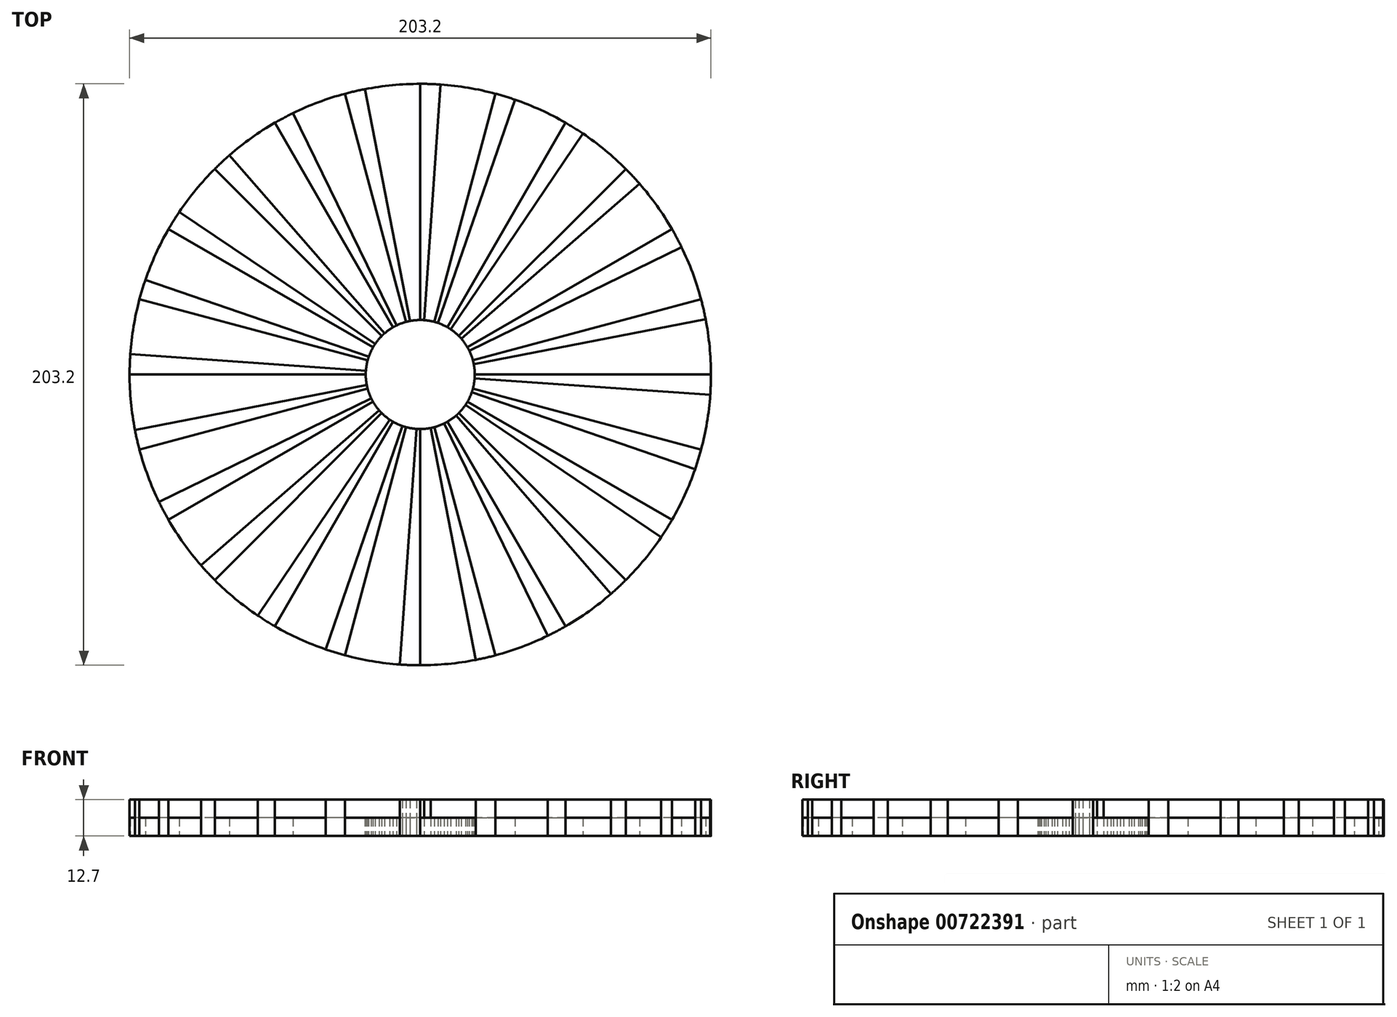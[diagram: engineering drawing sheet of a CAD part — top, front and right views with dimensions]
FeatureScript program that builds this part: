
annotation { "Feature Type Name" : "Feature", "Feature Type Description" : "" }
export const myFeature = defineFeature(function(context is Context, id is Id, definition is map)
    precondition{}
    {
        {
            var Q0;
            Q0=qCreatedBy(makeId("Top.planeOp"),FACE);
            var sketch = newSketch(context, id + "F0", { "sketchPlane" : qUnion([Q0])});
            skCircle(sketch, "E0", {"center": v(0, 0) * mm, "radius": 101.6 * mm});
            skLineSegment(sketch, "E1", {"start": v(0, 0) * mm, "end": v(0, 101.6) * mm});
            skLineSegment(sketch, "E2.1.0", {"start": v(0, 0) * mm, "end": v(-26.3, 98.14) * mm});
            skLineSegment(sketch, "E2.2.0", {"start": v(0, 0) * mm, "end": v(-50.8, 87.99) * mm});
            skLineSegment(sketch, "E2.3.0", {"start": v(0, 0) * mm, "end": v(-71.84, 71.84) * mm});
            skLineSegment(sketch, "E2.4.0", {"start": v(0, 0) * mm, "end": v(-87.99, 50.8) * mm});
            skLineSegment(sketch, "E2.5.0", {"start": v(0, 0) * mm, "end": v(-98.14, 26.3) * mm});
            skLineSegment(sketch, "E2.6.0", {"start": v(0, 0) * mm, "end": v(-101.6, 0) * mm});
            skLineSegment(sketch, "E2.7.0", {"start": v(0, 0) * mm, "end": v(-98.14, -26.3) * mm});
            skLineSegment(sketch, "E2.8.0", {"start": v(0, 0) * mm, "end": v(-87.99, -50.8) * mm});
            skLineSegment(sketch, "E2.9.0", {"start": v(0, 0) * mm, "end": v(-71.84, -71.84) * mm});
            skLineSegment(sketch, "E2.10.0", {"start": v(0, 0) * mm, "end": v(-50.8, -87.99) * mm});
            skLineSegment(sketch, "E2.11.0", {"start": v(0, 0) * mm, "end": v(-26.3, -98.14) * mm});
            skLineSegment(sketch, "E2.12.0", {"start": v(0, 0) * mm, "end": v(0, -101.6) * mm});
            skLineSegment(sketch, "E2.13.0", {"start": v(0, 0) * mm, "end": v(26.3, -98.14) * mm});
            skLineSegment(sketch, "E2.14.0", {"start": v(0, 0) * mm, "end": v(50.8, -87.99) * mm});
            skLineSegment(sketch, "E2.15.0", {"start": v(0, 0) * mm, "end": v(71.84, -71.84) * mm});
            skLineSegment(sketch, "E2.16.0", {"start": v(0, 0) * mm, "end": v(87.99, -50.8) * mm});
            skLineSegment(sketch, "E2.17.0", {"start": v(0, 0) * mm, "end": v(98.14, -26.3) * mm});
            skLineSegment(sketch, "E2.18.0", {"start": v(0, 0) * mm, "end": v(101.6, 0) * mm});
            skLineSegment(sketch, "E2.19.0", {"start": v(0, 0) * mm, "end": v(98.14, 26.3) * mm});
            skLineSegment(sketch, "E2.20.0", {"start": v(0, 0) * mm, "end": v(87.99, 50.8) * mm});
            skLineSegment(sketch, "E2.21.0", {"start": v(0, 0) * mm, "end": v(71.84, 71.84) * mm});
            skLineSegment(sketch, "E2.22.0", {"start": v(0, 0) * mm, "end": v(50.8, 87.99) * mm});
            skLineSegment(sketch, "E2.23.0", {"start": v(0, 0) * mm, "end": v(26.3, 98.14) * mm});
            skLineSegment(sketch, "E3.1.0", {"start": v(0, 0) * mm, "end": v(33.08, 96.06) * mm});
            skLineSegment(sketch, "E3.anchor1", {"start": v(0, 0) * mm, "end": v(26.3, 98.14) * mm, "construction": true});
            skLineSegment(sketch, "E3.anchor2", {"start": v(0, 0) * mm, "end": v(33.08, 96.06) * mm, "construction": true});
            skLineSegment(sketch, "E4.1.0", {"start": v(0, 0) * mm, "end": v(7.09, 101.35) * mm});
            skLineSegment(sketch, "E4.2.0", {"start": v(0, 0) * mm, "end": v(-19.39, 99.73) * mm});
            skLineSegment(sketch, "E4.3.0", {"start": v(0, 0) * mm, "end": v(-44.54, 91.32) * mm});
            skLineSegment(sketch, "E4.4.0", {"start": v(0, 0) * mm, "end": v(-66.66, 76.68) * mm});
            skLineSegment(sketch, "E4.5.0", {"start": v(0, 0) * mm, "end": v(-84.23, 56.81) * mm});
            skLineSegment(sketch, "E4.6.0", {"start": v(0, 0) * mm, "end": v(-96.06, 33.08) * mm});
            skLineSegment(sketch, "E4.7.0", {"start": v(0, 0) * mm, "end": v(-101.35, 7.09) * mm});
            skLineSegment(sketch, "E4.8.0", {"start": v(0, 0) * mm, "end": v(-99.73, -19.39) * mm});
            skLineSegment(sketch, "E4.9.0", {"start": v(0, 0) * mm, "end": v(-91.32, -44.54) * mm});
            skLineSegment(sketch, "E4.10.0", {"start": v(0, 0) * mm, "end": v(-76.68, -66.66) * mm});
            skLineSegment(sketch, "E4.11.0", {"start": v(0, 0) * mm, "end": v(-56.81, -84.23) * mm});
            skLineSegment(sketch, "E4.12.0", {"start": v(0, 0) * mm, "end": v(-33.08, -96.06) * mm});
            skLineSegment(sketch, "E4.13.0", {"start": v(0, 0) * mm, "end": v(-7.09, -101.35) * mm});
            skLineSegment(sketch, "E4.14.0", {"start": v(0, 0) * mm, "end": v(19.39, -99.73) * mm});
            skLineSegment(sketch, "E4.15.0", {"start": v(0, 0) * mm, "end": v(44.54, -91.32) * mm});
            skLineSegment(sketch, "E4.16.0", {"start": v(0, 0) * mm, "end": v(66.66, -76.68) * mm});
            skLineSegment(sketch, "E4.17.0", {"start": v(0, 0) * mm, "end": v(84.23, -56.81) * mm});
            skLineSegment(sketch, "E4.18.0", {"start": v(0, 0) * mm, "end": v(96.06, -33.08) * mm});
            skLineSegment(sketch, "E4.19.0", {"start": v(0, 0) * mm, "end": v(101.35, -7.09) * mm});
            skLineSegment(sketch, "E4.20.0", {"start": v(0, 0) * mm, "end": v(99.73, 19.39) * mm});
            skLineSegment(sketch, "E4.21.0", {"start": v(0, 0) * mm, "end": v(91.32, 44.54) * mm});
            skLineSegment(sketch, "E4.22.0", {"start": v(0, 0) * mm, "end": v(76.68, 66.66) * mm});
            skLineSegment(sketch, "E5.2.23.0", {"start": v(0, 0) * mm, "end": v(56.81, 84.23) * mm});
            skCircle(sketch, "E6", {"center": v(0, 0) * mm, "radius": 19.05 * mm});
            skSolve(sketch);
        }
        {
            var Q0;
            {var subQ0=sQuery(id+"F0.wireOp",EDGE,"E2.1.0");var subQ1=sQuery(id+"F0.wireOp",EDGE,"E0");var subQ2=makeQuery(id+"F0.imprint","INTERSECT",VERTEX,{"derivedFrom":[subQ1,subQ0]});Q0=makeQuery(id+"F0.imprint","IMPRINT",FACE,{"disambiguationData":[TD([[makeQuery(id+"F0.imprint","IMPRINT",EDGE,{"disambiguationData":[TD([[subQ2,1.0]])],"derivedFrom":subQ1}),1.0]])]});}
            var Q1;
            {var subQ0=sQuery(id+"F0.wireOp",EDGE,"E1");var subQ1=sQuery(id+"F0.wireOp",EDGE,"E0");var subQ2=makeQuery(id+"F0.imprint","INTERSECT",VERTEX,{"derivedFrom":[subQ1,subQ0]});Q1=makeQuery(id+"F0.imprint","IMPRINT",FACE,{"disambiguationData":[TD([[makeQuery(id+"F0.imprint","IMPRINT",EDGE,{"disambiguationData":[TD([[subQ2,1.0]])],"derivedFrom":subQ1}),1.0]])]});}
            var Q2;
            {var subQ0=sQuery(id+"F0.wireOp",EDGE,"E2.23.0");var subQ1=sQuery(id+"F0.wireOp",EDGE,"E0");var subQ2=makeQuery(id+"F0.imprint","INTERSECT",VERTEX,{"derivedFrom":[subQ1,subQ0]});Q2=makeQuery(id+"F0.imprint","IMPRINT",FACE,{"disambiguationData":[TD([[makeQuery(id+"F0.imprint","IMPRINT",EDGE,{"disambiguationData":[TD([[subQ2,1.0]])],"derivedFrom":subQ1}),1.0]])]});}
            var Q3;
            {var subQ0=sQuery(id+"F0.wireOp",EDGE,"E2.22.0");var subQ1=sQuery(id+"F0.wireOp",EDGE,"E0");var subQ2=makeQuery(id+"F0.imprint","INTERSECT",VERTEX,{"derivedFrom":[subQ1,subQ0]});Q3=makeQuery(id+"F0.imprint","IMPRINT",FACE,{"disambiguationData":[TD([[makeQuery(id+"F0.imprint","IMPRINT",EDGE,{"disambiguationData":[TD([[subQ2,1.0]])],"derivedFrom":subQ1}),1.0]])]});}
            var Q4;
            {var subQ0=sQuery(id+"F0.wireOp",EDGE,"E2.21.0");var subQ1=sQuery(id+"F0.wireOp",EDGE,"E0");var subQ2=makeQuery(id+"F0.imprint","INTERSECT",VERTEX,{"derivedFrom":[subQ1,subQ0]});Q4=makeQuery(id+"F0.imprint","IMPRINT",FACE,{"disambiguationData":[TD([[makeQuery(id+"F0.imprint","IMPRINT",EDGE,{"disambiguationData":[TD([[subQ2,1.0]])],"derivedFrom":subQ1}),1.0]])]});}
            var Q5;
            {var subQ0=sQuery(id+"F0.wireOp",EDGE,"E2.20.0");var subQ1=sQuery(id+"F0.wireOp",EDGE,"E0");var subQ2=makeQuery(id+"F0.imprint","INTERSECT",VERTEX,{"derivedFrom":[subQ1,subQ0]});Q5=makeQuery(id+"F0.imprint","IMPRINT",FACE,{"disambiguationData":[TD([[makeQuery(id+"F0.imprint","IMPRINT",EDGE,{"disambiguationData":[TD([[subQ2,1.0]])],"derivedFrom":subQ1}),1.0]])]});}
            var Q6;
            {var subQ0=sQuery(id+"F0.wireOp",EDGE,"E2.19.0");var subQ1=sQuery(id+"F0.wireOp",EDGE,"E0");var subQ2=makeQuery(id+"F0.imprint","INTERSECT",VERTEX,{"derivedFrom":[subQ1,subQ0]});Q6=makeQuery(id+"F0.imprint","IMPRINT",FACE,{"disambiguationData":[TD([[makeQuery(id+"F0.imprint","IMPRINT",EDGE,{"disambiguationData":[TD([[subQ2,1.0]])],"derivedFrom":subQ1}),1.0]])]});}
            var Q7;
            {var subQ0=sQuery(id+"F0.wireOp",EDGE,"E2.18.0");var subQ1=sQuery(id+"F0.wireOp",EDGE,"E0");var subQ2=makeQuery(id+"F0.imprint","INTERSECT",VERTEX,{"derivedFrom":[subQ1,subQ0]});Q7=makeQuery(id+"F0.imprint","IMPRINT",FACE,{"disambiguationData":[TD([[makeQuery(id+"F0.imprint","IMPRINT",EDGE,{"disambiguationData":[TD([[subQ2,1.0]])],"derivedFrom":subQ1}),1.0]])]});}
            var Q8;
            {var subQ0=sQuery(id+"F0.wireOp",EDGE,"E2.17.0");var subQ1=sQuery(id+"F0.wireOp",EDGE,"E0");var subQ2=makeQuery(id+"F0.imprint","INTERSECT",VERTEX,{"derivedFrom":[subQ1,subQ0]});Q8=makeQuery(id+"F0.imprint","IMPRINT",FACE,{"disambiguationData":[TD([[makeQuery(id+"F0.imprint","IMPRINT",EDGE,{"disambiguationData":[TD([[subQ2,1.0]])],"derivedFrom":subQ1}),1.0]])]});}
            var Q9;
            {var subQ0=sQuery(id+"F0.wireOp",EDGE,"E2.16.0");var subQ1=sQuery(id+"F0.wireOp",EDGE,"E0");var subQ2=makeQuery(id+"F0.imprint","INTERSECT",VERTEX,{"derivedFrom":[subQ1,subQ0]});Q9=makeQuery(id+"F0.imprint","IMPRINT",FACE,{"disambiguationData":[TD([[makeQuery(id+"F0.imprint","IMPRINT",EDGE,{"disambiguationData":[TD([[subQ2,1.0]])],"derivedFrom":subQ1}),1.0]])]});}
            var Q10;
            {var subQ0=sQuery(id+"F0.wireOp",EDGE,"E2.15.0");var subQ1=sQuery(id+"F0.wireOp",EDGE,"E0");var subQ2=makeQuery(id+"F0.imprint","INTERSECT",VERTEX,{"derivedFrom":[subQ1,subQ0]});Q10=makeQuery(id+"F0.imprint","IMPRINT",FACE,{"disambiguationData":[TD([[makeQuery(id+"F0.imprint","IMPRINT",EDGE,{"disambiguationData":[TD([[subQ2,1.0]])],"derivedFrom":subQ1}),1.0]])]});}
            var Q11;
            {var subQ0=sQuery(id+"F0.wireOp",EDGE,"E2.14.0");var subQ1=sQuery(id+"F0.wireOp",EDGE,"E0");var subQ2=makeQuery(id+"F0.imprint","INTERSECT",VERTEX,{"derivedFrom":[subQ1,subQ0]});Q11=makeQuery(id+"F0.imprint","IMPRINT",FACE,{"disambiguationData":[TD([[makeQuery(id+"F0.imprint","IMPRINT",EDGE,{"disambiguationData":[TD([[subQ2,1.0]])],"derivedFrom":subQ1}),1.0]])]});}
            var Q12;
            {var subQ0=sQuery(id+"F0.wireOp",EDGE,"E2.13.0");var subQ1=sQuery(id+"F0.wireOp",EDGE,"E0");var subQ2=makeQuery(id+"F0.imprint","INTERSECT",VERTEX,{"derivedFrom":[subQ1,subQ0]});Q12=makeQuery(id+"F0.imprint","IMPRINT",FACE,{"disambiguationData":[TD([[makeQuery(id+"F0.imprint","IMPRINT",EDGE,{"disambiguationData":[TD([[subQ2,1.0]])],"derivedFrom":subQ1}),1.0]])]});}
            var Q13;
            {var subQ0=sQuery(id+"F0.wireOp",EDGE,"E2.12.0");var subQ1=sQuery(id+"F0.wireOp",EDGE,"E0");var subQ2=makeQuery(id+"F0.imprint","INTERSECT",VERTEX,{"derivedFrom":[subQ1,subQ0]});Q13=makeQuery(id+"F0.imprint","IMPRINT",FACE,{"disambiguationData":[TD([[makeQuery(id+"F0.imprint","IMPRINT",EDGE,{"disambiguationData":[TD([[subQ2,1.0]])],"derivedFrom":subQ1}),1.0]])]});}
            var Q14;
            {var subQ0=sQuery(id+"F0.wireOp",EDGE,"E2.11.0");var subQ1=sQuery(id+"F0.wireOp",EDGE,"E0");var subQ2=makeQuery(id+"F0.imprint","INTERSECT",VERTEX,{"derivedFrom":[subQ1,subQ0]});Q14=makeQuery(id+"F0.imprint","IMPRINT",FACE,{"disambiguationData":[TD([[makeQuery(id+"F0.imprint","IMPRINT",EDGE,{"disambiguationData":[TD([[subQ2,1.0]])],"derivedFrom":subQ1}),1.0]])]});}
            var Q15;
            {var subQ0=sQuery(id+"F0.wireOp",EDGE,"E2.10.0");var subQ1=sQuery(id+"F0.wireOp",EDGE,"E0");var subQ2=makeQuery(id+"F0.imprint","INTERSECT",VERTEX,{"derivedFrom":[subQ1,subQ0]});Q15=makeQuery(id+"F0.imprint","IMPRINT",FACE,{"disambiguationData":[TD([[makeQuery(id+"F0.imprint","IMPRINT",EDGE,{"disambiguationData":[TD([[subQ2,1.0]])],"derivedFrom":subQ1}),1.0]])]});}
            var Q16;
            {var subQ0=sQuery(id+"F0.wireOp",EDGE,"E2.9.0");var subQ1=sQuery(id+"F0.wireOp",EDGE,"E0");var subQ2=makeQuery(id+"F0.imprint","INTERSECT",VERTEX,{"derivedFrom":[subQ1,subQ0]});Q16=makeQuery(id+"F0.imprint","IMPRINT",FACE,{"disambiguationData":[TD([[makeQuery(id+"F0.imprint","IMPRINT",EDGE,{"disambiguationData":[TD([[subQ2,1.0]])],"derivedFrom":subQ1}),1.0]])]});}
            var Q17;
            {var subQ0=sQuery(id+"F0.wireOp",EDGE,"E2.8.0");var subQ1=sQuery(id+"F0.wireOp",EDGE,"E0");var subQ2=makeQuery(id+"F0.imprint","INTERSECT",VERTEX,{"derivedFrom":[subQ1,subQ0]});Q17=makeQuery(id+"F0.imprint","IMPRINT",FACE,{"disambiguationData":[TD([[makeQuery(id+"F0.imprint","IMPRINT",EDGE,{"disambiguationData":[TD([[subQ2,1.0]])],"derivedFrom":subQ1}),1.0]])]});}
            var Q18;
            {var subQ0=sQuery(id+"F0.wireOp",EDGE,"E2.7.0");var subQ1=sQuery(id+"F0.wireOp",EDGE,"E0");var subQ2=makeQuery(id+"F0.imprint","INTERSECT",VERTEX,{"derivedFrom":[subQ1,subQ0]});Q18=makeQuery(id+"F0.imprint","IMPRINT",FACE,{"disambiguationData":[TD([[makeQuery(id+"F0.imprint","IMPRINT",EDGE,{"disambiguationData":[TD([[subQ2,1.0]])],"derivedFrom":subQ1}),1.0]])]});}
            var Q19;
            {var subQ0=sQuery(id+"F0.wireOp",EDGE,"E2.6.0");var subQ1=sQuery(id+"F0.wireOp",EDGE,"E0");var subQ2=makeQuery(id+"F0.imprint","INTERSECT",VERTEX,{"derivedFrom":[subQ1,subQ0]});Q19=makeQuery(id+"F0.imprint","IMPRINT",FACE,{"disambiguationData":[TD([[makeQuery(id+"F0.imprint","IMPRINT",EDGE,{"disambiguationData":[TD([[subQ2,1.0]])],"derivedFrom":subQ1}),1.0]])]});}
            var Q20;
            {var subQ0=sQuery(id+"F0.wireOp",EDGE,"E2.5.0");var subQ1=sQuery(id+"F0.wireOp",EDGE,"E0");var subQ2=makeQuery(id+"F0.imprint","INTERSECT",VERTEX,{"derivedFrom":[subQ1,subQ0]});Q20=makeQuery(id+"F0.imprint","IMPRINT",FACE,{"disambiguationData":[TD([[makeQuery(id+"F0.imprint","IMPRINT",EDGE,{"disambiguationData":[TD([[subQ2,1.0]])],"derivedFrom":subQ1}),1.0]])]});}
            var Q21;
            {var subQ0=sQuery(id+"F0.wireOp",EDGE,"E2.4.0");var subQ1=sQuery(id+"F0.wireOp",EDGE,"E0");var subQ2=makeQuery(id+"F0.imprint","INTERSECT",VERTEX,{"derivedFrom":[subQ1,subQ0]});Q21=makeQuery(id+"F0.imprint","IMPRINT",FACE,{"disambiguationData":[TD([[makeQuery(id+"F0.imprint","IMPRINT",EDGE,{"disambiguationData":[TD([[subQ2,1.0]])],"derivedFrom":subQ1}),1.0]])]});}
            var Q22;
            {var subQ0=sQuery(id+"F0.wireOp",EDGE,"E2.3.0");var subQ1=sQuery(id+"F0.wireOp",EDGE,"E0");var subQ2=makeQuery(id+"F0.imprint","INTERSECT",VERTEX,{"derivedFrom":[subQ1,subQ0]});Q22=makeQuery(id+"F0.imprint","IMPRINT",FACE,{"disambiguationData":[TD([[makeQuery(id+"F0.imprint","IMPRINT",EDGE,{"disambiguationData":[TD([[subQ2,1.0]])],"derivedFrom":subQ1}),1.0]])]});}
            var Q23;
            {var subQ0=sQuery(id+"F0.wireOp",EDGE,"E2.2.0");var subQ1=sQuery(id+"F0.wireOp",EDGE,"E0");var subQ2=makeQuery(id+"F0.imprint","INTERSECT",VERTEX,{"derivedFrom":[subQ1,subQ0]});Q23=makeQuery(id+"F0.imprint","IMPRINT",FACE,{"disambiguationData":[TD([[makeQuery(id+"F0.imprint","IMPRINT",EDGE,{"disambiguationData":[TD([[subQ2,1.0]])],"derivedFrom":subQ1}),1.0]])]});}
            extrude(context, id + "F1", {"entities" : qUnion([Q0, Q1, Q2, Q3, Q4, Q5, Q6, Q7, Q8, Q9, Q10, Q11, Q12, Q13, Q14, Q15, Q16, Q17, Q18, Q19, Q20, Q21, Q22, Q23]), "depth" : 12.7 * mm, "offsetDistance" : 25.4 * mm});
        }
        {
            var Q0;
            {var subQ0=sQuery(id+"F0.wireOp",EDGE,"E2.5.0");var subQ1=sQuery(id+"F0.wireOp",EDGE,"E0");var subQ2=makeQuery(id+"F0.imprint","INTERSECT",VERTEX,{"derivedFrom":[subQ1,subQ0]});Q0=makeQuery(id+"F0.imprint","IMPRINT",FACE,{"disambiguationData":[TD([[makeQuery(id+"F0.imprint","IMPRINT",EDGE,{"disambiguationData":[TD([[subQ2,-1.0]])],"derivedFrom":subQ1}),1.0]])]});}
            var Q1;
            {var subQ0=sQuery(id+"F0.wireOp",EDGE,"E2.4.0");var subQ1=sQuery(id+"F0.wireOp",EDGE,"E0");var subQ2=makeQuery(id+"F0.imprint","INTERSECT",VERTEX,{"derivedFrom":[subQ1,subQ0]});Q1=makeQuery(id+"F0.imprint","IMPRINT",FACE,{"disambiguationData":[TD([[makeQuery(id+"F0.imprint","IMPRINT",EDGE,{"disambiguationData":[TD([[subQ2,-1.0]])],"derivedFrom":subQ1}),1.0]])]});}
            var Q2;
            {var subQ0=sQuery(id+"F0.wireOp",EDGE,"E2.3.0");var subQ1=sQuery(id+"F0.wireOp",EDGE,"E0");var subQ2=makeQuery(id+"F0.imprint","INTERSECT",VERTEX,{"derivedFrom":[subQ1,subQ0]});Q2=makeQuery(id+"F0.imprint","IMPRINT",FACE,{"disambiguationData":[TD([[makeQuery(id+"F0.imprint","IMPRINT",EDGE,{"disambiguationData":[TD([[subQ2,-1.0]])],"derivedFrom":subQ1}),1.0]])]});}
            var Q3;
            {var subQ0=sQuery(id+"F0.wireOp",EDGE,"E2.2.0");var subQ1=sQuery(id+"F0.wireOp",EDGE,"E0");var subQ2=makeQuery(id+"F0.imprint","INTERSECT",VERTEX,{"derivedFrom":[subQ1,subQ0]});Q3=makeQuery(id+"F0.imprint","IMPRINT",FACE,{"disambiguationData":[TD([[makeQuery(id+"F0.imprint","IMPRINT",EDGE,{"disambiguationData":[TD([[subQ2,-1.0]])],"derivedFrom":subQ1}),1.0]])]});}
            var Q4;
            {var subQ0=sQuery(id+"F0.wireOp",EDGE,"E2.1.0");var subQ1=sQuery(id+"F0.wireOp",EDGE,"E0");var subQ2=makeQuery(id+"F0.imprint","INTERSECT",VERTEX,{"derivedFrom":[subQ1,subQ0]});Q4=makeQuery(id+"F0.imprint","IMPRINT",FACE,{"disambiguationData":[TD([[makeQuery(id+"F0.imprint","IMPRINT",EDGE,{"disambiguationData":[TD([[subQ2,-1.0]])],"derivedFrom":subQ1}),1.0]])]});}
            var Q5;
            {var subQ0=sQuery(id+"F0.wireOp",EDGE,"E1");var subQ1=sQuery(id+"F0.wireOp",EDGE,"E0");var subQ2=makeQuery(id+"F0.imprint","INTERSECT",VERTEX,{"derivedFrom":[subQ1,subQ0]});Q5=makeQuery(id+"F0.imprint","IMPRINT",FACE,{"disambiguationData":[TD([[makeQuery(id+"F0.imprint","IMPRINT",EDGE,{"disambiguationData":[TD([[subQ2,-1.0]])],"derivedFrom":subQ1}),1.0]])]});}
            var Q6;
            {var subQ0=sQuery(id+"F0.wireOp",EDGE,"E2.23.0");var subQ1=sQuery(id+"F0.wireOp",EDGE,"E0");var subQ2=makeQuery(id+"F0.imprint","INTERSECT",VERTEX,{"derivedFrom":[subQ1,subQ0]});Q6=makeQuery(id+"F0.imprint","IMPRINT",FACE,{"disambiguationData":[TD([[makeQuery(id+"F0.imprint","IMPRINT",EDGE,{"disambiguationData":[TD([[subQ2,-1.0]])],"derivedFrom":subQ1}),1.0]])]});}
            var Q7;
            {var subQ0=sQuery(id+"F0.wireOp",EDGE,"E2.6.0");var subQ1=sQuery(id+"F0.wireOp",EDGE,"E0");var subQ2=makeQuery(id+"F0.imprint","INTERSECT",VERTEX,{"derivedFrom":[subQ1,subQ0]});Q7=makeQuery(id+"F0.imprint","IMPRINT",FACE,{"disambiguationData":[TD([[makeQuery(id+"F0.imprint","IMPRINT",EDGE,{"disambiguationData":[TD([[subQ2,-1.0]])],"derivedFrom":subQ1}),1.0]])]});}
            var Q8;
            {var subQ0=sQuery(id+"F0.wireOp",EDGE,"E2.7.0");var subQ1=sQuery(id+"F0.wireOp",EDGE,"E0");var subQ2=makeQuery(id+"F0.imprint","INTERSECT",VERTEX,{"derivedFrom":[subQ1,subQ0]});Q8=makeQuery(id+"F0.imprint","IMPRINT",FACE,{"disambiguationData":[TD([[makeQuery(id+"F0.imprint","IMPRINT",EDGE,{"disambiguationData":[TD([[subQ2,-1.0]])],"derivedFrom":subQ1}),1.0]])]});}
            var Q9;
            {var subQ0=sQuery(id+"F0.wireOp",EDGE,"E2.8.0");var subQ1=sQuery(id+"F0.wireOp",EDGE,"E0");var subQ2=makeQuery(id+"F0.imprint","INTERSECT",VERTEX,{"derivedFrom":[subQ1,subQ0]});Q9=makeQuery(id+"F0.imprint","IMPRINT",FACE,{"disambiguationData":[TD([[makeQuery(id+"F0.imprint","IMPRINT",EDGE,{"disambiguationData":[TD([[subQ2,-1.0]])],"derivedFrom":subQ1}),1.0]])]});}
            var Q10;
            {var subQ0=sQuery(id+"F0.wireOp",EDGE,"E2.9.0");var subQ1=sQuery(id+"F0.wireOp",EDGE,"E0");var subQ2=makeQuery(id+"F0.imprint","INTERSECT",VERTEX,{"derivedFrom":[subQ1,subQ0]});Q10=makeQuery(id+"F0.imprint","IMPRINT",FACE,{"disambiguationData":[TD([[makeQuery(id+"F0.imprint","IMPRINT",EDGE,{"disambiguationData":[TD([[subQ2,-1.0]])],"derivedFrom":subQ1}),1.0]])]});}
            var Q11;
            {var subQ0=sQuery(id+"F0.wireOp",EDGE,"E2.10.0");var subQ1=sQuery(id+"F0.wireOp",EDGE,"E0");var subQ2=makeQuery(id+"F0.imprint","INTERSECT",VERTEX,{"derivedFrom":[subQ1,subQ0]});Q11=makeQuery(id+"F0.imprint","IMPRINT",FACE,{"disambiguationData":[TD([[makeQuery(id+"F0.imprint","IMPRINT",EDGE,{"disambiguationData":[TD([[subQ2,-1.0]])],"derivedFrom":subQ1}),1.0]])]});}
            var Q12;
            {var subQ0=sQuery(id+"F0.wireOp",EDGE,"E2.11.0");var subQ1=sQuery(id+"F0.wireOp",EDGE,"E0");var subQ2=makeQuery(id+"F0.imprint","INTERSECT",VERTEX,{"derivedFrom":[subQ1,subQ0]});Q12=makeQuery(id+"F0.imprint","IMPRINT",FACE,{"disambiguationData":[TD([[makeQuery(id+"F0.imprint","IMPRINT",EDGE,{"disambiguationData":[TD([[subQ2,-1.0]])],"derivedFrom":subQ1}),1.0]])]});}
            var Q13;
            {var subQ0=sQuery(id+"F0.wireOp",EDGE,"E2.12.0");var subQ1=sQuery(id+"F0.wireOp",EDGE,"E0");var subQ2=makeQuery(id+"F0.imprint","INTERSECT",VERTEX,{"derivedFrom":[subQ1,subQ0]});Q13=makeQuery(id+"F0.imprint","IMPRINT",FACE,{"disambiguationData":[TD([[makeQuery(id+"F0.imprint","IMPRINT",EDGE,{"disambiguationData":[TD([[subQ2,-1.0]])],"derivedFrom":subQ1}),1.0]])]});}
            var Q14;
            {var subQ0=sQuery(id+"F0.wireOp",EDGE,"E2.13.0");var subQ1=sQuery(id+"F0.wireOp",EDGE,"E0");var subQ2=makeQuery(id+"F0.imprint","INTERSECT",VERTEX,{"derivedFrom":[subQ1,subQ0]});Q14=makeQuery(id+"F0.imprint","IMPRINT",FACE,{"disambiguationData":[TD([[makeQuery(id+"F0.imprint","IMPRINT",EDGE,{"disambiguationData":[TD([[subQ2,-1.0]])],"derivedFrom":subQ1}),1.0]])]});}
            var Q15;
            {var subQ0=sQuery(id+"F0.wireOp",EDGE,"E2.14.0");var subQ1=sQuery(id+"F0.wireOp",EDGE,"E0");var subQ2=makeQuery(id+"F0.imprint","INTERSECT",VERTEX,{"derivedFrom":[subQ1,subQ0]});Q15=makeQuery(id+"F0.imprint","IMPRINT",FACE,{"disambiguationData":[TD([[makeQuery(id+"F0.imprint","IMPRINT",EDGE,{"disambiguationData":[TD([[subQ2,-1.0]])],"derivedFrom":subQ1}),1.0]])]});}
            var Q16;
            {var subQ0=sQuery(id+"F0.wireOp",EDGE,"E2.15.0");var subQ1=sQuery(id+"F0.wireOp",EDGE,"E0");var subQ2=makeQuery(id+"F0.imprint","INTERSECT",VERTEX,{"derivedFrom":[subQ1,subQ0]});Q16=makeQuery(id+"F0.imprint","IMPRINT",FACE,{"disambiguationData":[TD([[makeQuery(id+"F0.imprint","IMPRINT",EDGE,{"disambiguationData":[TD([[subQ2,-1.0]])],"derivedFrom":subQ1}),1.0]])]});}
            var Q17;
            {var subQ0=sQuery(id+"F0.wireOp",EDGE,"E2.16.0");var subQ1=sQuery(id+"F0.wireOp",EDGE,"E0");var subQ2=makeQuery(id+"F0.imprint","INTERSECT",VERTEX,{"derivedFrom":[subQ1,subQ0]});Q17=makeQuery(id+"F0.imprint","IMPRINT",FACE,{"disambiguationData":[TD([[makeQuery(id+"F0.imprint","IMPRINT",EDGE,{"disambiguationData":[TD([[subQ2,-1.0]])],"derivedFrom":subQ1}),1.0]])]});}
            var Q18;
            {var subQ0=sQuery(id+"F0.wireOp",EDGE,"E2.17.0");var subQ1=sQuery(id+"F0.wireOp",EDGE,"E0");var subQ2=makeQuery(id+"F0.imprint","INTERSECT",VERTEX,{"derivedFrom":[subQ1,subQ0]});Q18=makeQuery(id+"F0.imprint","IMPRINT",FACE,{"disambiguationData":[TD([[makeQuery(id+"F0.imprint","IMPRINT",EDGE,{"disambiguationData":[TD([[subQ2,-1.0]])],"derivedFrom":subQ1}),1.0]])]});}
            var Q19;
            {var subQ0=sQuery(id+"F0.wireOp",EDGE,"E2.18.0");var subQ1=sQuery(id+"F0.wireOp",EDGE,"E0");var subQ2=makeQuery(id+"F0.imprint","INTERSECT",VERTEX,{"derivedFrom":[subQ1,subQ0]});Q19=makeQuery(id+"F0.imprint","IMPRINT",FACE,{"disambiguationData":[TD([[makeQuery(id+"F0.imprint","IMPRINT",EDGE,{"disambiguationData":[TD([[subQ2,-1.0]])],"derivedFrom":subQ1}),1.0]])]});}
            var Q20;
            {var subQ0=sQuery(id+"F0.wireOp",EDGE,"E2.19.0");var subQ1=sQuery(id+"F0.wireOp",EDGE,"E0");var subQ2=makeQuery(id+"F0.imprint","INTERSECT",VERTEX,{"derivedFrom":[subQ1,subQ0]});Q20=makeQuery(id+"F0.imprint","IMPRINT",FACE,{"disambiguationData":[TD([[makeQuery(id+"F0.imprint","IMPRINT",EDGE,{"disambiguationData":[TD([[subQ2,-1.0]])],"derivedFrom":subQ1}),1.0]])]});}
            var Q21;
            {var subQ0=sQuery(id+"F0.wireOp",EDGE,"E2.20.0");var subQ1=sQuery(id+"F0.wireOp",EDGE,"E0");var subQ2=makeQuery(id+"F0.imprint","INTERSECT",VERTEX,{"derivedFrom":[subQ1,subQ0]});Q21=makeQuery(id+"F0.imprint","IMPRINT",FACE,{"disambiguationData":[TD([[makeQuery(id+"F0.imprint","IMPRINT",EDGE,{"disambiguationData":[TD([[subQ2,-1.0]])],"derivedFrom":subQ1}),1.0]])]});}
            var Q22;
            {var subQ0=sQuery(id+"F0.wireOp",EDGE,"E2.21.0");var subQ1=sQuery(id+"F0.wireOp",EDGE,"E0");var subQ2=makeQuery(id+"F0.imprint","INTERSECT",VERTEX,{"derivedFrom":[subQ1,subQ0]});Q22=makeQuery(id+"F0.imprint","IMPRINT",FACE,{"disambiguationData":[TD([[makeQuery(id+"F0.imprint","IMPRINT",EDGE,{"disambiguationData":[TD([[subQ2,-1.0]])],"derivedFrom":subQ1}),1.0]])]});}
            var Q23;
            {var subQ0=sQuery(id+"F0.wireOp",EDGE,"E2.22.0");var subQ1=sQuery(id+"F0.wireOp",EDGE,"E0");var subQ2=makeQuery(id+"F0.imprint","INTERSECT",VERTEX,{"derivedFrom":[subQ1,subQ0]});Q23=makeQuery(id+"F0.imprint","IMPRINT",FACE,{"disambiguationData":[TD([[makeQuery(id+"F0.imprint","IMPRINT",EDGE,{"disambiguationData":[TD([[subQ2,-1.0]])],"derivedFrom":subQ1}),1.0]])]});}
            extrude(context, id + "F2", {"entities" : qUnion([Q0, Q1, Q2, Q3, Q4, Q5, Q6, Q7, Q8, Q9, Q10, Q11, Q12, Q13, Q14, Q15, Q16, Q17, Q18, Q19, Q20, Q21, Q22, Q23]), "depth" : 6.35 * mm, "offsetDistance" : 25.4 * mm});
        }
    });
